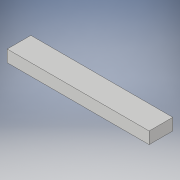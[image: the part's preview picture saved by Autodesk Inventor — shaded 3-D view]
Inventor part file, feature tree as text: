
AUTODESK INVENTOR PART (.ipt)
format: ipt  version: 2018 (Build 220112000, 112)  size: 90,112 bytes
history: native  units: in
note: dims shown in document units (in); Inventor stores cm internally (conversion verified against a paired STEP export)
features: extrude x1, sketch x1
ambient origin geometry x8: Origin, YZ Plane, XZ Plane, XY Plane, X Axis, Y Axis, Z Axis, Center Point
bodies: Solid1 (feature_tree)
feature tree (2):
  extrude  "Extrusion1"  Depth=2.0in
  sketch  "Sketch1"  dims[d0=1.0in d1=2.0in d2=12.0in d3=0.0in]
